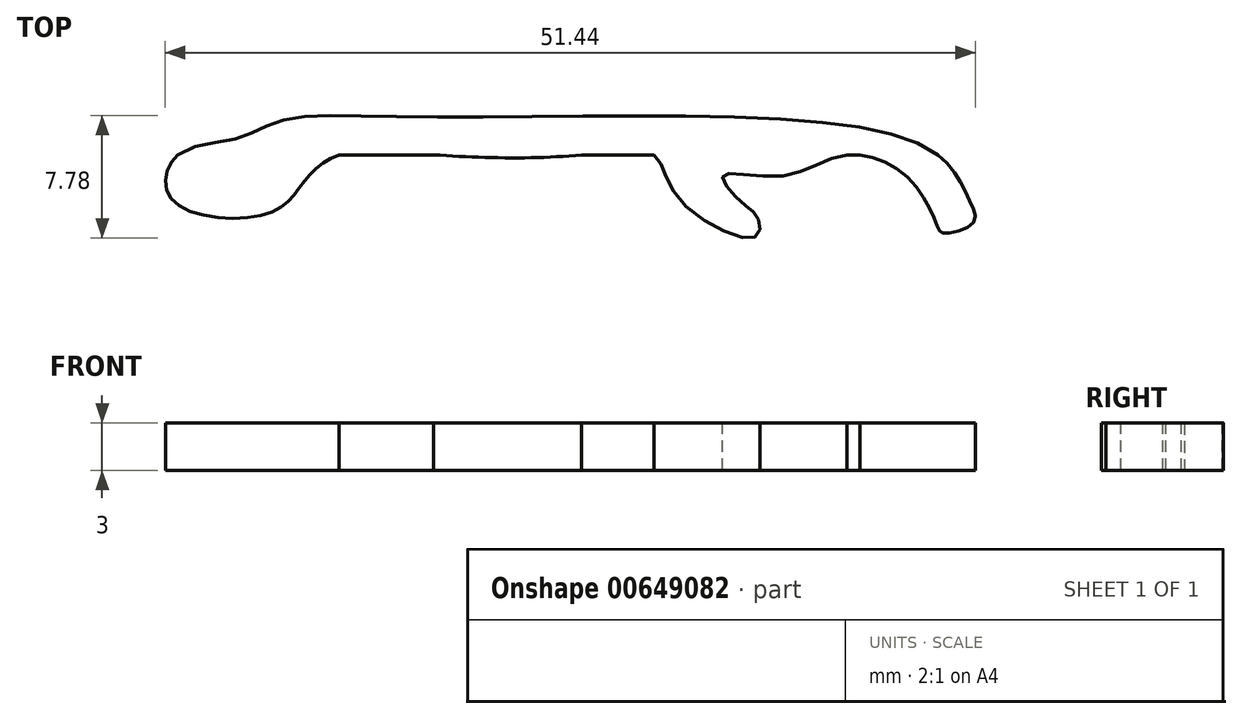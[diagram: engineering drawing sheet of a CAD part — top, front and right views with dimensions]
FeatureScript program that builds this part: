
annotation { "Feature Type Name" : "Feature", "Feature Type Description" : "" }
export const myFeature = defineFeature(function(context is Context, id is Id, definition is map)
    precondition{}
    {
        {
            var Q0;
            Q0=qCreatedBy(makeId("Top.planeOp"),FACE);
            var sketch = newSketch(context, id + "F0", { "sketchPlane" : qUnion([Q0])});
            skFitSpline(sketch, "E0", {"points": [v(-16.47, 1.03) * mm, v(-13.72, 2.16) * mm, v(-5.6, 2.4) * mm, v(17.78, 2.28) * mm, v(28.04, 0) * mm, v(30.04, -2.84) * mm, v(30.29, -4.34) * mm, v(28.41, -4.97) * mm, v(28.04, -4.6) * mm, v(26.41, -1.72) * mm, v(22.29, 0) * mm, v(18.16, -1.34) * mm, v(14.4, -1.34) * mm, v(15.53, -2.97) * mm, v(16.66, -4.1) * mm, v(16.4, -5.22) * mm, v(11.53, -2.72) * mm, v(10.03, 0) * mm, v(5.4, 0) * mm, v(-3.97, 0) * mm, v(-9.97, 0) * mm, v(-12.22, -1.72) * mm, v(-14.47, -3.72) * mm, v(-20.6, -2.84) * mm, v(-20.22, 0) * mm, v(-16.47, 1.03) * mm]});
            skLineSegment(sketch, "E1", {"start": v(-20.22, 0) * mm, "end": v(28.04, 0) * mm});
            skSolve(sketch);
        }
        {
            var Q0;
            Q0 = qSketchRegion(id + "F0", true);
            extrude(context, id + "F1", {"entities" : qUnion([Q0]), "depth" : 3 * mm, "offsetDistance" : 25.4 * mm});
        }
    });
